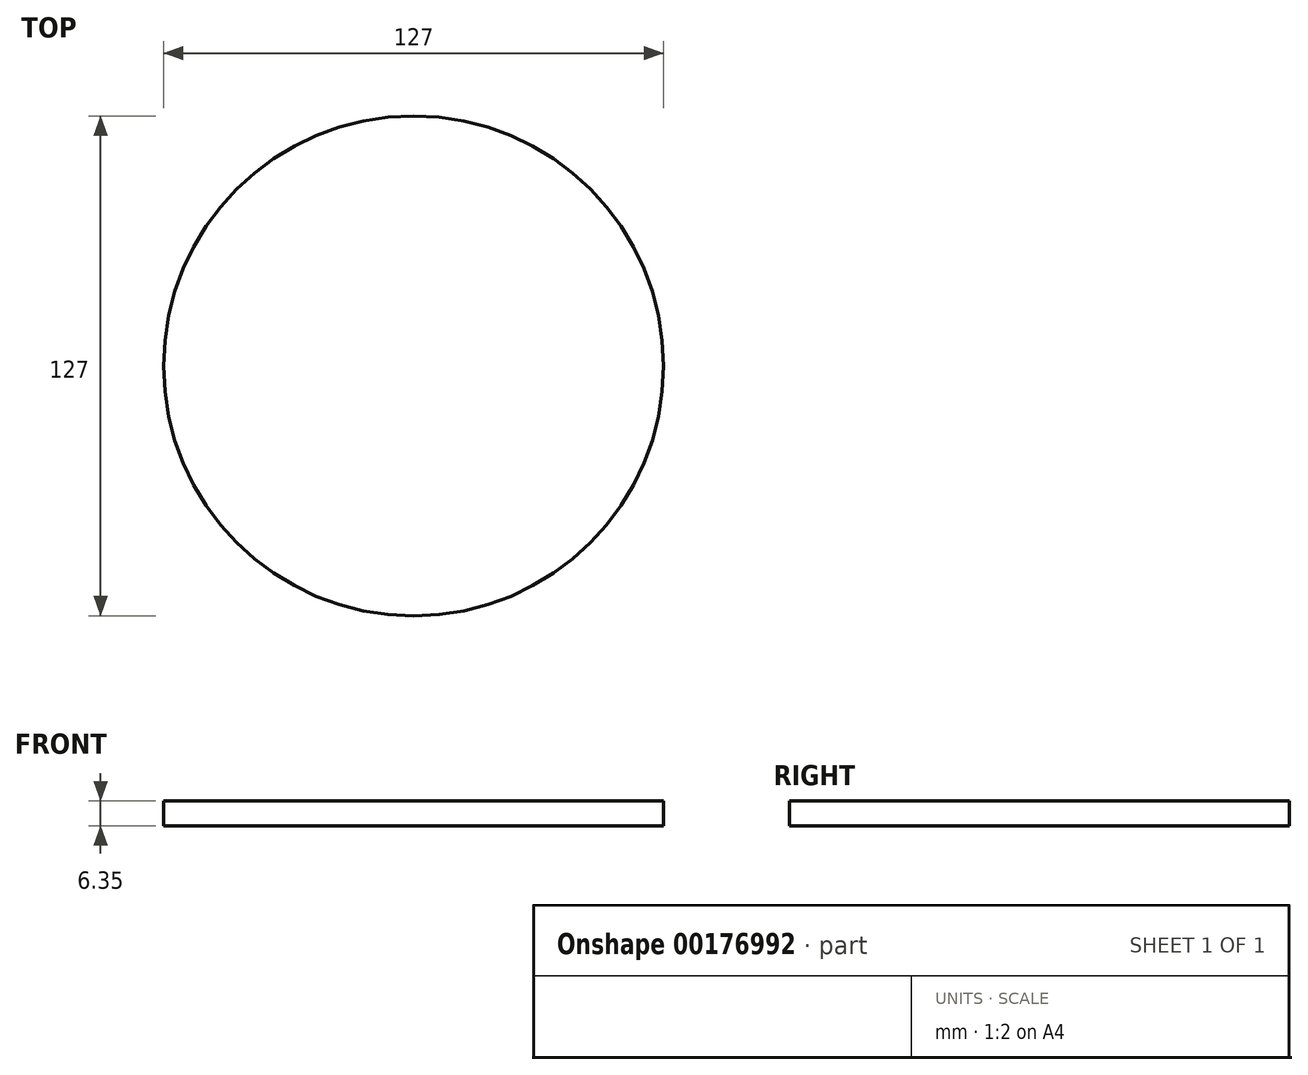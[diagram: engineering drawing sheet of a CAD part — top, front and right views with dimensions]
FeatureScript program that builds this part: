
annotation { "Feature Type Name" : "Feature", "Feature Type Description" : "" }
export const myFeature = defineFeature(function(context is Context, id is Id, definition is map)
    precondition{}
    {
        {
            var Q0;
            Q0=qCreatedBy(makeId("Top.planeOp"),FACE);
            var sketch = newSketch(context, id + "F0", { "sketchPlane" : qUnion([Q0])});
            skCircle(sketch, "E0", {"center": v(0, 0) * mm, "radius": 63.5 * mm});
            skSolve(sketch);
        }
        {
            var Q0;
            Q0 = qSketchRegion(id + "F0", true);
            extrude(context, id + "F1", {"entities" : qUnion([Q0]), "depth" : 6.35 * mm});
        }
    });
